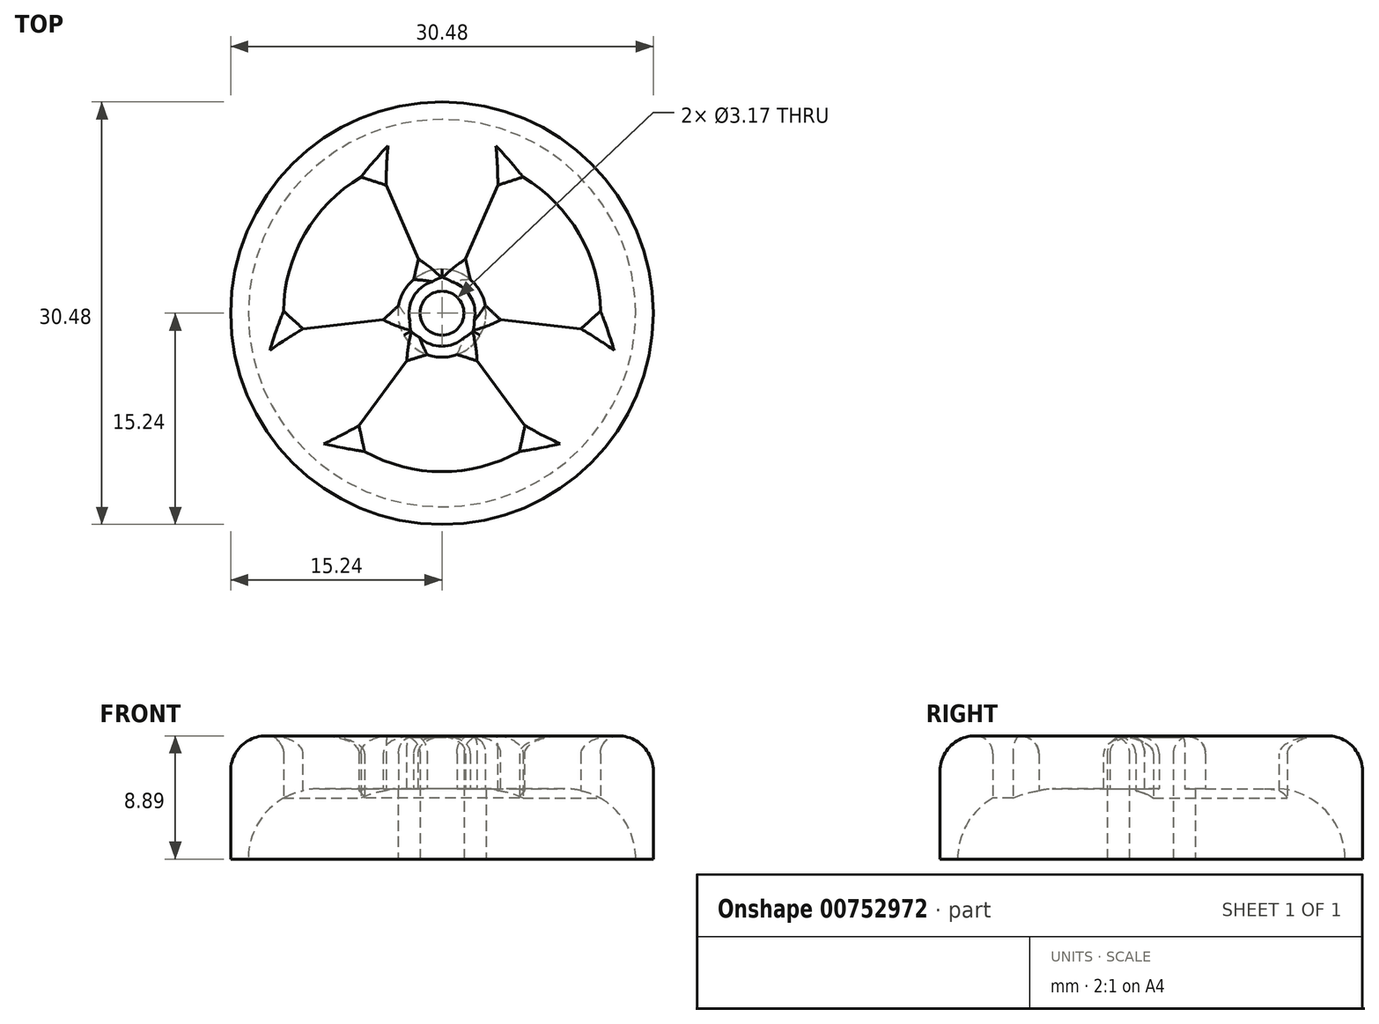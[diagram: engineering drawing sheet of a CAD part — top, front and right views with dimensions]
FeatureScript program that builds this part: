
annotation { "Feature Type Name" : "Feature", "Feature Type Description" : "" }
export const myFeature = defineFeature(function(context is Context, id is Id, definition is map)
    precondition{}
    {
        {
            var Q0;
            Q0=qCreatedBy(makeId("Top.planeOp"),FACE);
            var sketch = newSketch(context, id + "F0", { "sketchPlane" : qUnion([Q0])});
            skCircle(sketch, "E0", {"center": v(0, 0) * mm, "radius": 15.24 * mm});
            skArc(sketch, "E1", {"start": v(-4.57, 10.48) * mm, "mid": v(-9.9, 5.71) * mm, "end": v(-11.36, -1.28) * mm});
            skArc(sketch, "E2", {"start": v(-1.89, -2.55) * mm, "mid": v(0, -3.18) * mm, "end": v(1.89, -2.55) * mm});
            skLineSegment(sketch, "E3", {"start": v(-4.57, 10.48) * mm, "end": v(-1.27, 2.9) * mm});
            skLineSegment(sketch, "E4", {"start": v(1.27, 2.9) * mm, "end": v(4.57, 10.48) * mm});
            skLineSegment(sketch, "E5", {"start": v(-1.27, 2.9) * mm, "end": v(0, 0) * mm, "construction": true});
            skLineSegment(sketch, "E6", {"start": v(1.27, 2.9) * mm, "end": v(0, 0) * mm, "construction": true});
            skLineSegment(sketch, "E7", {"start": v(-1.27, 2.9) * mm, "end": v(1.27, 2.9) * mm, "construction": true});
            skLineSegment(sketch, "E8", {"start": v(-4.57, 10.48) * mm, "end": v(4.57, 10.48) * mm, "construction": true});
            skLineSegment(sketch, "E9.1.0", {"start": v(-6.79, -9.2) * mm, "end": v(-1.89, -2.55) * mm});
            skLineSegment(sketch, "E9.1.1", {"start": v(-3.16, -0.36) * mm, "end": v(-11.36, -1.28) * mm});
            skLineSegment(sketch, "E9.2.0", {"start": v(11.36, -1.28) * mm, "end": v(3.16, -0.36) * mm});
            skLineSegment(sketch, "E9.2.1", {"start": v(1.89, -2.55) * mm, "end": v(6.79, -9.2) * mm});
            skArc(sketch, "E10.trimOffspring", {"start": v(-1.27, 2.9) * mm, "mid": v(-2.75, 1.59) * mm, "end": v(-3.16, -0.36) * mm});
            skArc(sketch, "E11.trimOffspring", {"start": v(3.16, -0.36) * mm, "mid": v(2.75, 1.59) * mm, "end": v(1.27, 2.9) * mm});
            skArc(sketch, "E12.trimOffspring", {"start": v(11.36, -1.28) * mm, "mid": v(9.9, 5.72) * mm, "end": v(4.57, 10.48) * mm});
            skArc(sketch, "E13.trimOffspring", {"start": v(-6.79, -9.2) * mm, "mid": v(0, -11.43) * mm, "end": v(6.79, -9.2) * mm});
            skSolve(sketch);
        }
        {
            var Q0;
            Q0 = qSketchRegion(id + "F0", true);
            extrude(context, id + "F1", {"entities" : qUnion([Q0]), "depth" : 8.9 * mm, "offsetDistance" : 25.4 * mm});
        }
        {
            var Q0;
            Q0=makeQuery(id+"F1.opExtrude","CAP_EDGE",EDGE,{"disambiguationData":[OSD([sQuery(id+"F0.wireOp",EDGE,"E0")])],"isStart":false});
            fillet(context, id + "F2", {"entities" : qUnion([Q0]), "radius" : 2.54 * mm, "tangentPropagation" : true, "allowEdgeOverflow" : false});
        }
        {
            var Q0;
            Q0=makeQuery(id+"F0.imprint","IMPRINT",FACE,{"disambiguationData":[TD([[makeQuery(id+"F0.imprint","IMPRINT",EDGE,{"derivedFrom":sQuery(id+"F0.wireOp",EDGE,"E0")}),1.0]])]});
            var sketch = newSketch(context, id + "F3", { "sketchPlane" : qUnion([Q0])});
            skCircle(sketch, "E14", {"center": v(0, 0) * mm, "radius": 13.97 * mm});
            skCircle(sketch, "E15", {"center": v(0, 0) * mm, "radius": 3.18 * mm});
            skSolve(sketch);
        }
        {
            var Q0;
            Q0 = qSketchRegion(id + "F3", true);
            extrude(context, id + "F4", {"entities" : qUnion([Q0]), "operationType" : NewBodyOperationType.REMOVE, "depth" : 5.08 * mm, "offsetDistance" : 25.4 * mm});
        }
        {
            var Q0;
            {var subQ0=sQuery(id+"F0.wireOp",EDGE,"E2");var subQ1=sQuery(id+"F0.wireOp",EDGE,"E10.trimOffspring");var subQ2=sQuery(id+"F0.wireOp",EDGE,"E11.trimOffspring");Q0=makeQuery(id+"F4.boolean.opBoolean","SPLIT",FACE,{"disambiguationData":[TD([makeQuery(id+"F1.opExtrude","SWEPT_FACE",FACE,{"disambiguationData":[OSD([subQ0])]})])],"derivedFrom":makeQuery(id+"F1.opExtrude","CAP_FACE",FACE,{"disambiguationData":[OSD([sQuery(id+"F0.wireOp",EDGE,"E0"),sQuery(id+"F0.wireOp",EDGE,"E1"),subQ0,sQuery(id+"F0.wireOp",EDGE,"E3"),sQuery(id+"F0.wireOp",EDGE,"E4"),sQuery(id+"F0.wireOp",EDGE,"E9.1.0"),sQuery(id+"F0.wireOp",EDGE,"E9.1.1"),sQuery(id+"F0.wireOp",EDGE,"E9.2.0"),sQuery(id+"F0.wireOp",EDGE,"E9.2.1"),subQ1,subQ2,sQuery(id+"F0.wireOp",EDGE,"E12.trimOffspring"),sQuery(id+"F0.wireOp",EDGE,"E13.trimOffspring")])],"isStart":true})});}
            var sketch = newSketch(context, id + "F5", { "sketchPlane" : qUnion([Q0])});
            skCircle(sketch, "E16", {"center": v(0, 0) * mm, "radius": 1.59 * mm});
            skSolve(sketch);
        }
        {
            var Q0;
            Q0 = qSketchRegion(id + "F5", true);
            extrude(context, id + "F6", {"entities" : qUnion([Q0]), "operationType" : NewBodyOperationType.REMOVE, "oppositeDirection" : true, "depth" : 25.4 * mm, "offsetDistance" : 25.4 * mm});
        }
        {
            var Q0;
            Q0=makeQuery(id+"F1.opExtrude","CAP_FACE",FACE,{"disambiguationData":[OSD([sQuery(id+"F0.wireOp",EDGE,"E0"),sQuery(id+"F0.wireOp",EDGE,"E1"),sQuery(id+"F0.wireOp",EDGE,"E2"),sQuery(id+"F0.wireOp",EDGE,"E3"),sQuery(id+"F0.wireOp",EDGE,"E4"),sQuery(id+"F0.wireOp",EDGE,"E9.1.0"),sQuery(id+"F0.wireOp",EDGE,"E9.1.1"),sQuery(id+"F0.wireOp",EDGE,"E9.2.0"),sQuery(id+"F0.wireOp",EDGE,"E9.2.1"),sQuery(id+"F0.wireOp",EDGE,"E10.trimOffspring"),sQuery(id+"F0.wireOp",EDGE,"E11.trimOffspring"),sQuery(id+"F0.wireOp",EDGE,"E12.trimOffspring"),sQuery(id+"F0.wireOp",EDGE,"E13.trimOffspring")])],"isStart":false});
            fillet(context, id + "F7", {"entities" : qUnion([Q0]), "radius" : 1.27 * mm, "tangentPropagation" : true, "allowEdgeOverflow" : false});
        }
        {
            var Q0;
            Q0=makeQuery(id+"F4.boolean.opBoolean","COPY",EDGE,{"derivedFrom":makeQuery(id+"F4.opExtrude","CAP_EDGE",EDGE,{"disambiguationData":[OSD([sQuery(id+"F3.wireOp",EDGE,"E14")])],"isStart":false})});
            fillet(context, id + "F8", {"entities" : qUnion([Q0]), "radius" : 5.08 * mm, "tangentPropagation" : true, "allowEdgeOverflow" : false});
        }
        {
            var Q0;
            Q0=makeQuery(id+"F1.opExtrude","SWEPT_EDGE",EDGE,{"disambiguationData":[OSD([sQuery(id+"F0.wireOp",EDGE,"E9.1.1"),sQuery(id+"F0.wireOp",EDGE,"E10.trimOffspring")])]});
            var Q1;
            Q1=makeQuery(id+"F1.opExtrude","SWEPT_EDGE",EDGE,{"disambiguationData":[OSD([sQuery(id+"F0.wireOp",EDGE,"E3"),sQuery(id+"F0.wireOp",EDGE,"E10.trimOffspring")])]});
            var Q2;
            Q2=makeQuery(id+"F1.opExtrude","SWEPT_EDGE",EDGE,{"disambiguationData":[OSD([sQuery(id+"F0.wireOp",EDGE,"E2"),sQuery(id+"F0.wireOp",EDGE,"E9.1.0")])]});
            var Q3;
            Q3=makeQuery(id+"F1.opExtrude","SWEPT_EDGE",EDGE,{"disambiguationData":[OSD([sQuery(id+"F0.wireOp",EDGE,"E2"),sQuery(id+"F0.wireOp",EDGE,"E9.2.1")])]});
            var Q4;
            Q4=makeQuery(id+"F1.opExtrude","SWEPT_EDGE",EDGE,{"disambiguationData":[OSD([sQuery(id+"F0.wireOp",EDGE,"E9.2.0"),sQuery(id+"F0.wireOp",EDGE,"E11.trimOffspring")])]});
            var Q5;
            Q5=makeQuery(id+"F1.opExtrude","SWEPT_EDGE",EDGE,{"disambiguationData":[OSD([sQuery(id+"F0.wireOp",EDGE,"E4"),sQuery(id+"F0.wireOp",EDGE,"E11.trimOffspring")])]});
            var Q6;
            Q6=makeQuery(id+"F1.opExtrude","SWEPT_EDGE",EDGE,{"disambiguationData":[OSD([sQuery(id+"F0.wireOp",EDGE,"E9.1.0"),sQuery(id+"F0.wireOp",EDGE,"E13.trimOffspring")])]});
            var Q7;
            Q7=makeQuery(id+"F1.opExtrude","SWEPT_EDGE",EDGE,{"disambiguationData":[OSD([sQuery(id+"F0.wireOp",EDGE,"E1"),sQuery(id+"F0.wireOp",EDGE,"E9.1.1")])]});
            var Q8;
            Q8=makeQuery(id+"F1.opExtrude","SWEPT_EDGE",EDGE,{"disambiguationData":[OSD([sQuery(id+"F0.wireOp",EDGE,"E1"),sQuery(id+"F0.wireOp",EDGE,"E3")])]});
            var Q9;
            Q9=makeQuery(id+"F1.opExtrude","SWEPT_EDGE",EDGE,{"disambiguationData":[OSD([sQuery(id+"F0.wireOp",EDGE,"E4"),sQuery(id+"F0.wireOp",EDGE,"E12.trimOffspring")])]});
            var Q10;
            Q10=makeQuery(id+"F1.opExtrude","SWEPT_EDGE",EDGE,{"disambiguationData":[OSD([sQuery(id+"F0.wireOp",EDGE,"E9.2.0"),sQuery(id+"F0.wireOp",EDGE,"E12.trimOffspring")])]});
            var Q11;
            Q11=makeQuery(id+"F1.opExtrude","SWEPT_EDGE",EDGE,{"disambiguationData":[OSD([sQuery(id+"F0.wireOp",EDGE,"E9.2.1"),sQuery(id+"F0.wireOp",EDGE,"E13.trimOffspring")])]});
            chamfer(context, id + "F9", {"entities" : qUnion([Q0, Q1, Q2, Q3, Q4, Q5, Q6, Q7, Q8, Q9, Q10, Q11]), "width" : 1.27 * mm, "tangentPropagation" : true});
        }
    });
